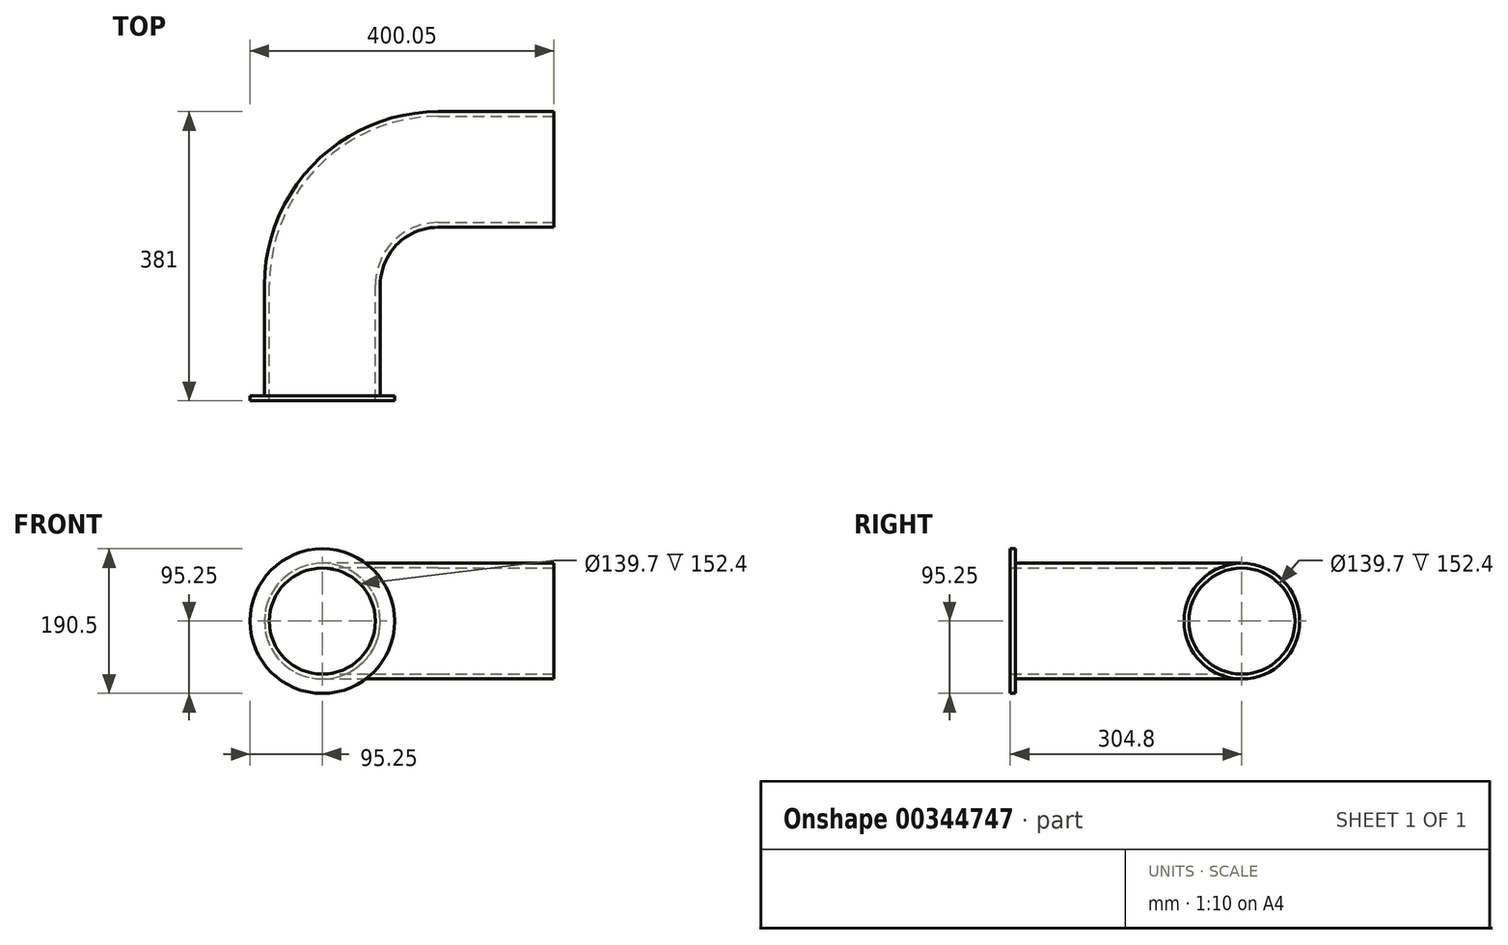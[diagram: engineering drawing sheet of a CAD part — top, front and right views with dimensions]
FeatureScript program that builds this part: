
annotation { "Feature Type Name" : "Feature", "Feature Type Description" : "" }
export const myFeature = defineFeature(function(context is Context, id is Id, definition is map)
    precondition{}
    {
        {
            var Q0;
            Q0=qCreatedBy(makeId("Front.planeOp"),FACE);
            var sketch = newSketch(context, id + "F0", { "sketchPlane" : qUnion([Q0])});
            skCircle(sketch, "E0", {"center": v(0, 0) * mm, "radius": 76.2 * mm});
            skCircle(sketch, "E1", {"center": v(0, 0) * mm, "radius": 95.25 * mm});
            skSolve(sketch);
        }
        {
            var Q0;
            Q0=qCreatedBy(makeId("Top.planeOp"),FACE);
            var sketch = newSketch(context, id + "F1", { "sketchPlane" : qUnion([Q0])});
            skLineSegment(sketch, "E2", {"start": v(0, 0) * mm, "end": v(0, 152.4) * mm});
            skLineSegment(sketch, "E3", {"start": v(152.4, 304.8) * mm, "end": v(304.8, 304.8) * mm});
            skPoint(sketch, "E4.visualSharp", {"position": v(0, 304.8) * mm});
            skArc(sketch, "E4.filletArc", {"start": v(152.4, 304.8) * mm, "mid": v(44.64, 260.16) * mm, "end": v(0, 152.4) * mm});
            skSolve(sketch);
        }
        {
            var Q0;
            Q0=makeQuery(id+"F0.imprint","IMPRINT",FACE,{"disambiguationData":[TD([[makeQuery(id+"F0.imprint","IMPRINT",EDGE,{"derivedFrom":sQuery(id+"F0.wireOp",EDGE,"E0")}),1.0]])]});
            var Q1;
            Q1=sQuery(id+"F1.wireOp",EDGE,"E2");
            var Q2;
            Q2=sQuery(id+"F1.wireOp",EDGE,"E4.filletArc");
            var Q3;
            Q3=sQuery(id+"F1.wireOp",EDGE,"E3");
            sweep(context, id + "F2", {"profiles" : qUnion([Q0]), "path" : qUnion([Q1, Q2, Q3])});
        }
        {
            var Q0;
            Q0=makeQuery(id+"F2.opSweep","CAP_FACE",FACE,{"disambiguationData":[OSD([sQuery(id+"F0.wireOp",EDGE,"E0"),sQuery(id+"F1.wireOp",VERTEX,"E2.start")])],"isStart":true});
            var Q1;
            Q1=makeQuery(id+"F2.opSweep","CAP_FACE",FACE,{"disambiguationData":[OSD([sQuery(id+"F0.wireOp",EDGE,"E0"),sQuery(id+"F1.wireOp",VERTEX,"E3.end")])],"isStart":false});
            var Q2;
            Q2=makeQuery(id+"F2.opSweep","SWEPT_BODY",BODY,{"disambiguationData":[OSD([sQuery(id+"F0.wireOp",EDGE,"E0"),sQuery(id+"F1.wireOp",EDGE,"E3")])]});
            shell(context, id + "F3", {"entities" : qUnion([Q0, Q1]), "parts" : qUnion([Q2]), "thickness" : 6.35 * mm});
        }
        {
            var Q0;
            Q0=makeQuery(id+"F0.imprint","IMPRINT",FACE,{"disambiguationData":[TD([[makeQuery(id+"F0.imprint","IMPRINT",EDGE,{"derivedFrom":sQuery(id+"F0.wireOp",EDGE,"E0")}),-1.0]])]});
            extrude(context, id + "F4", {"entities" : qUnion([Q0]), "operationType" : NewBodyOperationType.ADD, "depth" : -6.35 * mm});
        }
        {
            var Q0;
            Q0=sQuery(id+"F1.wireOp",VERTEX,"E3.end");
            var Q1;
            Q1=sQuery(id+"F1.wireOp",EDGE,"E3");
            cPlane(context, id + "F5", {"entities" : qUnion([Q0, Q1]), "cplaneType" : CPlaneType.LINE_POINT, "offset" : 25.4 * mm, "width" : 152.4 * mm, "height" : 152.4 * mm});
        }
    });
